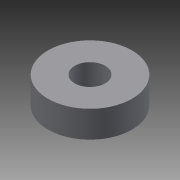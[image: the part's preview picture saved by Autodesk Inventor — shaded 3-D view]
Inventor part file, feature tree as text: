
AUTODESK INVENTOR PART (.ipt)
format: ipt  version: 2013 (Build 170138000, 138)  size: 73,216 bytes
history: native  units: mm
features: extrude x1, sketch x1
ambient origin geometry x8: Origin, YZ Plane, XZ Plane, XY Plane, X Axis, Y Axis, Z Axis, Center Point
bodies: Solid1 (feature_tree)
feature tree (2):
  extrude  "Extrusion1"  Depth=8.0mm
  sketch  "Sketch1"  dims[d0=22.0mm d2=8.0mm d3=7.0mm d4=0.0mm]
